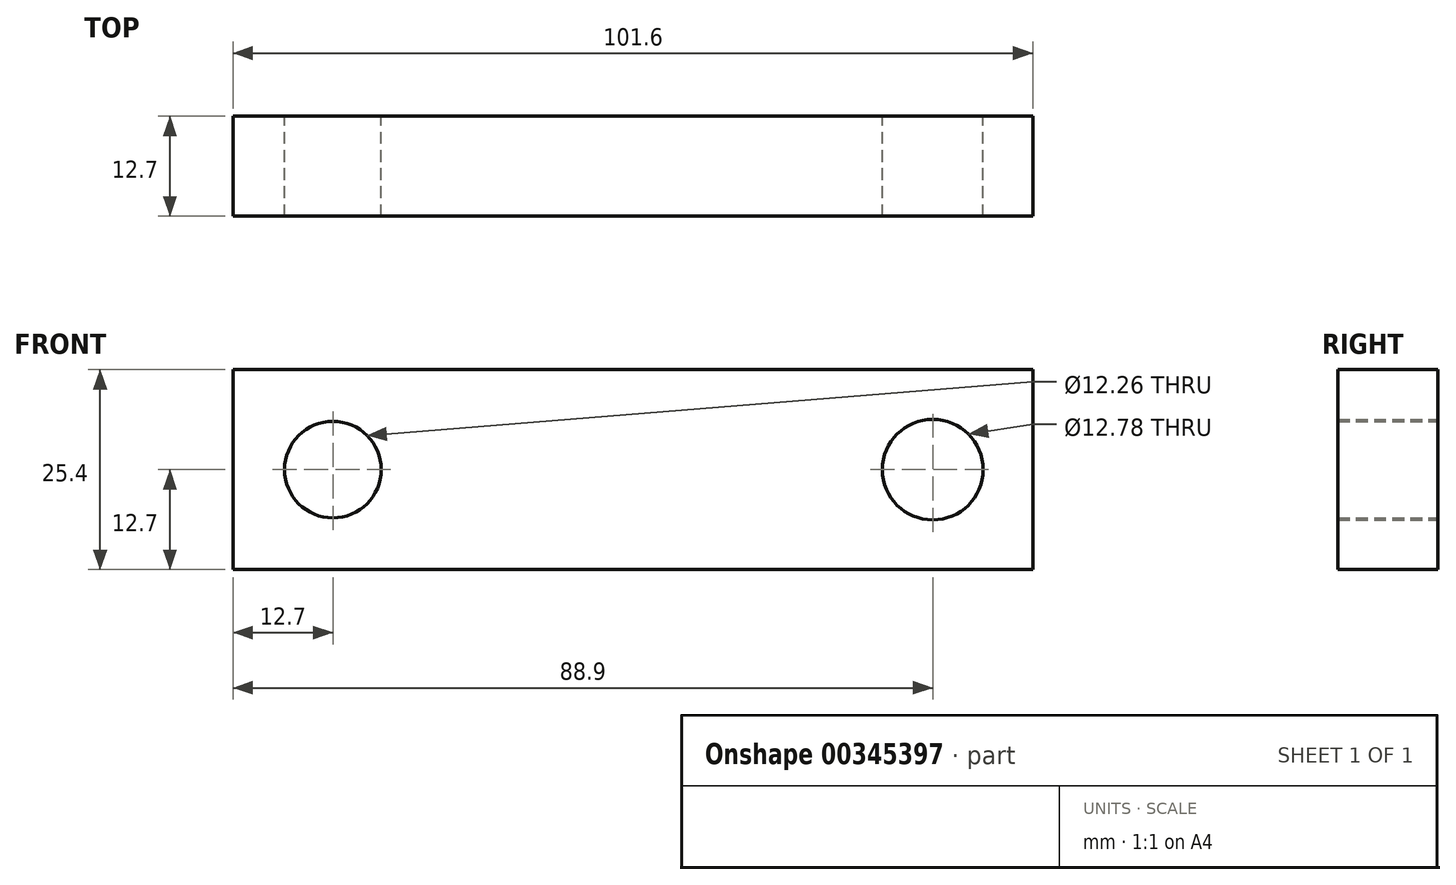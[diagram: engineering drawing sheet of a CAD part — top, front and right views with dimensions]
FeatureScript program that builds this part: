
annotation { "Feature Type Name" : "Feature", "Feature Type Description" : "" }
export const myFeature = defineFeature(function(context is Context, id is Id, definition is map)
    precondition{}
    {
        {
            var Q0;
            Q0=qCreatedBy(makeId("Front.planeOp"),FACE);
            var sketch = newSketch(context, id + "F0", { "sketchPlane" : qUnion([Q0])});
            skLineSegment(sketch, "E0.bottom", {"start": v(-12.7, 12.7) * mm, "end": v(88.9, 12.7) * mm});
            skLineSegment(sketch, "E0.top", {"start": v(-12.7, -12.7) * mm, "end": v(88.9, -12.7) * mm});
            skLineSegment(sketch, "E0.left", {"start": v(-12.7, 12.7) * mm, "end": v(-12.7, -12.7) * mm});
            skLineSegment(sketch, "E0.right", {"start": v(88.9, 12.7) * mm, "end": v(88.9, -12.7) * mm});
            skCircle(sketch, "E1", {"center": v(0, 0) * mm, "radius": 6.13 * mm});
            skCircle(sketch, "E2", {"center": v(76.2, 0) * mm, "radius": 6.4 * mm});
            skSolve(sketch);
        }
        {
            var Q0;
            Q0=makeQuery(id+"F0.imprint","IMPRINT",FACE,{"disambiguationData":[TD([[makeQuery(id+"F0.imprint","IMPRINT",EDGE,{"derivedFrom":sQuery(id+"F0.wireOp",EDGE,"E0.bottom")}),-1.0]])]});
            extrude(context, id + "F1", {"entities" : qUnion([Q0]), "depth" : 12.7 * mm});
        }
    });
